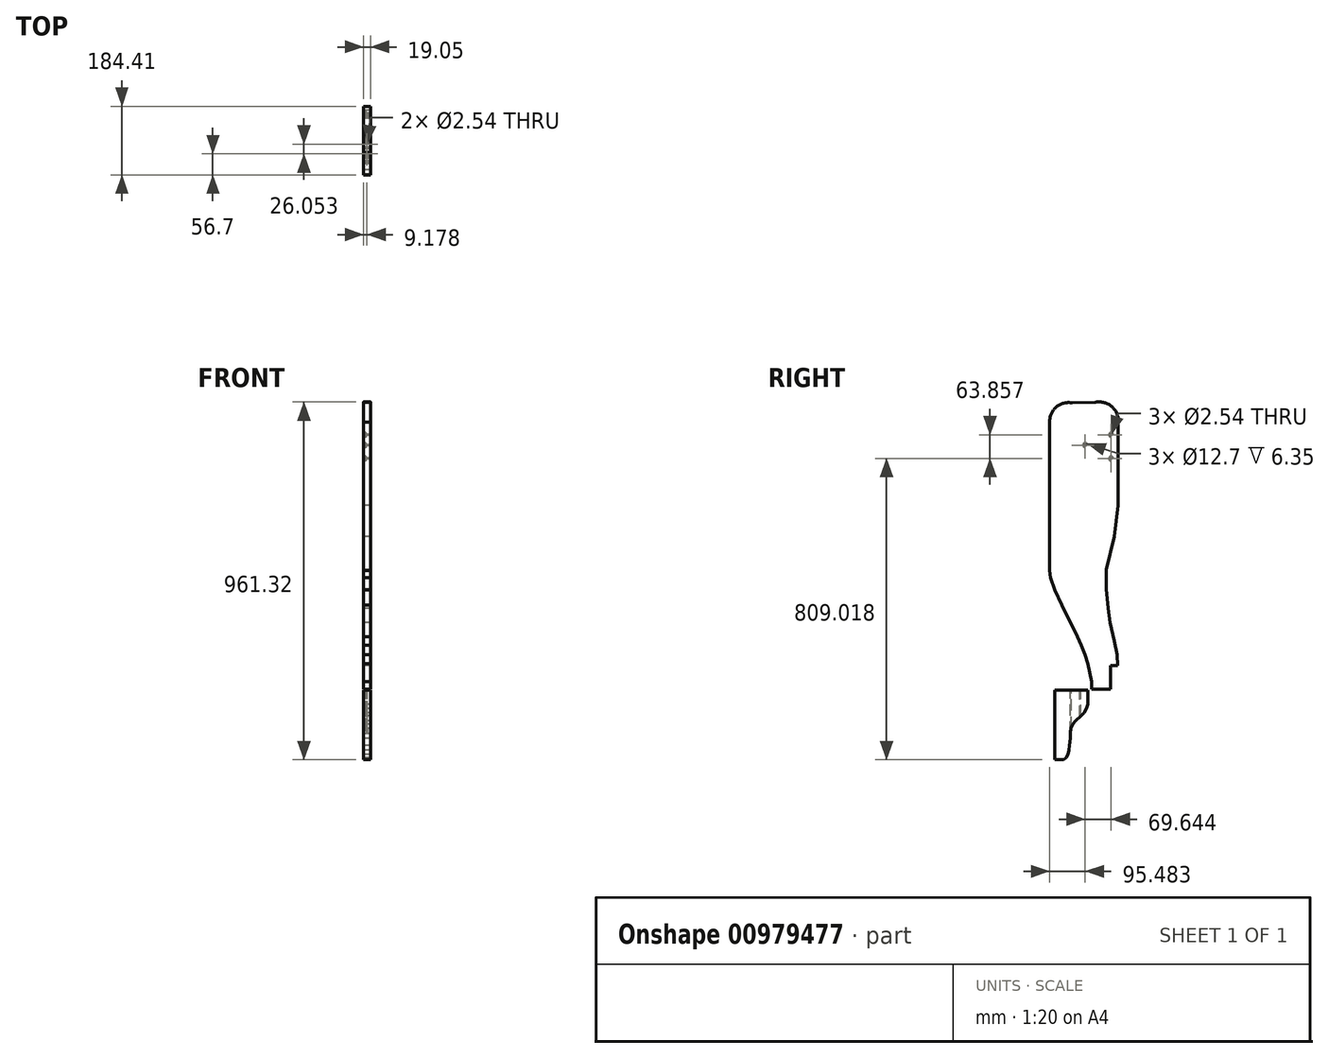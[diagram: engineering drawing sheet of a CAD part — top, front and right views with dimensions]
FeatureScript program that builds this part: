
annotation { "Feature Type Name" : "Feature", "Feature Type Description" : "" }
export const myFeature = defineFeature(function(context is Context, id is Id, definition is map)
    precondition{}
    {
        {
            var Q0;
            Q0=qCreatedBy(makeId("Right.planeOp"),FACE);
            var sketch = newSketch(context, id + "F0", { "sketchPlane" : qUnion([Q0])});
            skArc(sketch, "E0", {"start": v(-9.46, 75.88) * mm, "mid": v(-26, 118.46) * mm, "end": v(-70.06, 130.54) * mm});
            skArc(sketch, "E1", {"start": v(-132.5, 128.84) * mm, "mid": v(-175.59, 117.94) * mm, "end": v(-193.61, 77.32) * mm});
            skLineSegment(sketch, "E2", {"start": v(-70.06, 130.54) * mm, "end": v(-132.5, 128.84) * mm});
            skLineSegment(sketch, "E3", {"start": v(-9.46, -145.88) * mm, "end": v(-9.46, 75.88) * mm});
            skLineSegment(sketch, "E4", {"start": v(-193.61, 77.32) * mm, "end": v(-193.61, -321.25) * mm});
            skLineSegment(sketch, "E5", {"start": v(-10.8, -577.01) * mm, "end": v(-29.84, -577.01) * mm});
            skLineSegment(sketch, "E6", {"start": v(-9.46, -145.88) * mm, "end": v(-19.66, -230.65) * mm});
            skLineSegment(sketch, "E7", {"start": v(-19.66, -230.65) * mm, "end": v(-41.21, -318.93) * mm});
            skLineSegment(sketch, "E8", {"start": v(-41.21, -318.93) * mm, "end": v(-41.21, -370.76) * mm});
            skLineSegment(sketch, "E9", {"start": v(-41.21, -370.76) * mm, "end": v(-36.8, -423.85) * mm});
            skLineSegment(sketch, "E10", {"start": v(-36.8, -423.85) * mm, "end": v(-30.98, -461.78) * mm});
            skLineSegment(sketch, "E11", {"start": v(-30.98, -461.78) * mm, "end": v(-20.05, -510.64) * mm});
            skLineSegment(sketch, "E12", {"start": v(-20.05, -510.64) * mm, "end": v(-12.2, -547.2) * mm});
            skLineSegment(sketch, "E13", {"start": v(-12.2, -547.2) * mm, "end": v(-10.8, -577.01) * mm});
            skLineSegment(sketch, "E14", {"start": v(-29.84, -640.51) * mm, "end": v(-29.84, -577.01) * mm});
            skLineSegment(sketch, "E15", {"start": v(-87.3, -588.8) * mm, "end": v(-91.04, -571.55) * mm});
            skLineSegment(sketch, "E16", {"start": v(-91.04, -571.55) * mm, "end": v(-98.51, -548.28) * mm});
            skLineSegment(sketch, "E17", {"start": v(-98.51, -548.28) * mm, "end": v(-108.2, -522.94) * mm});
            skLineSegment(sketch, "E18", {"start": v(-108.2, -522.94) * mm, "end": v(-119.14, -499.02) * mm});
            skLineSegment(sketch, "E19", {"start": v(-119.14, -499.02) * mm, "end": v(-161.16, -414.63) * mm});
            skLineSegment(sketch, "E20", {"start": v(-161.16, -414.63) * mm, "end": v(-179.94, -373.8) * mm});
            skLineSegment(sketch, "E21", {"start": v(-179.94, -373.8) * mm, "end": v(-190.87, -340.66) * mm});
            skLineSegment(sketch, "E22", {"start": v(-190.87, -340.66) * mm, "end": v(-193.61, -321.25) * mm});
            skLineSegment(sketch, "E23", {"start": v(-101.28, 129.69) * mm, "end": v(-98.16, 15.43) * mm, "construction": true});
            skLineSegment(sketch, "E24", {"start": v(-98.16, 15.43) * mm, "end": v(-9.46, 17.85) * mm, "construction": true});
            skLineSegment(sketch, "E25", {"start": v(-9.46, 43.1) * mm, "end": v(-28.51, 43.1) * mm, "construction": true});
            skPoint(sketch, "E26", {"position": v(-28.34, 17.34) * mm});
            skPoint(sketch, "E27", {"position": v(-53.8, 16.64) * mm});
            skPoint(sketch, "E28", {"position": v(-88.41, 15.7) * mm});
            skPoint(sketch, "E29", {"position": v(-28.51, -20.76) * mm});
            skLineSegment(sketch, "E30", {"start": v(-98.16, 15.43) * mm, "end": v(-193.61, 12.83) * mm, "construction": true});
            skLineSegment(sketch, "E31", {"start": v(-193.61, 12.83) * mm, "end": v(-142.83, 14.21) * mm});
            skPoint(sketch, "E32", {"position": v(-142.83, 14.21) * mm});
            skLineSegment(sketch, "E33", {"start": v(-87.3, -588.8) * mm, "end": v(-80.64, -619.55) * mm});
            skLineSegment(sketch, "E34", {"start": v(-80.64, -619.55) * mm, "end": v(-80.64, -619.82) * mm});
            skLineSegment(sketch, "E35", {"start": v(-80.64, -619.82) * mm, "end": v(-80.64, -629.6) * mm});
            skLineSegment(sketch, "E36", {"start": v(-80.64, -629.6) * mm, "end": v(-80.64, -640.44) * mm});
            skLineSegment(sketch, "E37", {"start": v(-80.64, -640.44) * mm, "end": v(-29.84, -640.51) * mm});
            skSolve(sketch);
        }
        {
            var Q0;
            Q0=qSketchRegion(id+"F0",true);
            extrude(context, id + "F1", {"entities" : qUnion([Q0]), "depth" : 19.05 * mm});
        }
        {
            var Q0;
            Q0=qCreatedBy(makeId("Right.planeOp"),FACE);
            var sketch = newSketch(context, id + "F2", { "sketchPlane" : qUnion([Q0])});
            skLineSegment(sketch, "E38", {"start": v(-91.54, -643.6) * mm, "end": v(-180.44, -643.6) * mm});
            skLineSegment(sketch, "E39", {"start": v(-180.44, -643.6) * mm, "end": v(-180.44, -829.78) * mm});
            skLineSegment(sketch, "E40", {"start": v(-180.44, -829.78) * mm, "end": v(-163.7, -829.78) * mm});
            skLineSegment(sketch, "E41", {"start": v(-91.54, -643.6) * mm, "end": v(-91.54, -681.07) * mm});
            skLineSegment(sketch, "E42", {"start": v(-91.54, -681.07) * mm, "end": v(-94.58, -691.9) * mm});
            skLineSegment(sketch, "E43", {"start": v(-94.58, -691.9) * mm, "end": v(-101.21, -703.64) * mm});
            skLineSegment(sketch, "E44", {"start": v(-101.21, -703.64) * mm, "end": v(-108.9, -711.93) * mm});
            skLineSegment(sketch, "E45", {"start": v(-108.9, -711.93) * mm, "end": v(-123.5, -725.03) * mm});
            skLineSegment(sketch, "E46", {"start": v(-123.5, -725.03) * mm, "end": v(-131.33, -734.22) * mm});
            skLineSegment(sketch, "E47", {"start": v(-131.33, -734.22) * mm, "end": v(-136.6, -745.78) * mm});
            skLineSegment(sketch, "E48", {"start": v(-136.6, -745.78) * mm, "end": v(-138.5, -759.4) * mm});
            skLineSegment(sketch, "E49", {"start": v(-138.5, -759.4) * mm, "end": v(-138.5, -773.04) * mm});
            skLineSegment(sketch, "E50", {"start": v(-138.5, -773.04) * mm, "end": v(-140.18, -791.2) * mm});
            skLineSegment(sketch, "E51", {"start": v(-140.18, -791.2) * mm, "end": v(-142.1, -803.88) * mm});
            skLineSegment(sketch, "E52", {"start": v(-142.1, -803.88) * mm, "end": v(-144.72, -815.35) * mm});
            skLineSegment(sketch, "E53", {"start": v(-144.72, -815.35) * mm, "end": v(-149.5, -824.2) * mm});
            skLineSegment(sketch, "E54", {"start": v(-149.5, -824.2) * mm, "end": v(-155.48, -829.46) * mm});
            skLineSegment(sketch, "E55", {"start": v(-155.48, -829.46) * mm, "end": v(-163.7, -829.78) * mm});
            skSolve(sketch);
        }
        {
            var Q0;
            Q0=qSketchRegion(id+"F2",true);
            extrude(context, id + "F3", {"entities" : qUnion([Q0]), "depth" : 19.05 * mm});
        }
        {
            var Q0;
            Q0=makeQuery(id+"F3.opExtrude","SWEPT_FACE",FACE,{"disambiguationData":[OSD([sQuery(id+"F2.wireOp",EDGE,"E38")])]});
            var sketch = newSketch(context, id + "F4", { "sketchPlane" : qUnion([Q0])});
            skPoint(sketch, "E56", {"position": v(9.18, -110.89) * mm});
            skPoint(sketch, "E57", {"position": v(9.18, -136.94) * mm});
            skLineSegment(sketch, "E58", {"start": v(9.53, -180.44) * mm, "end": v(9.18, -91.54) * mm, "construction": true});
            skSolve(sketch);
        }
        {
            var Q0;
            Q0=sQuery(id+"F4.wireOp",VERTEX,"E57");
            var Q1;
            Q1=sQuery(id+"F4.wireOp",VERTEX,"E56");
            var Q2;
            Q2=makeQuery(id+"F3.opExtrude","SWEPT_BODY",BODY,{"disambiguationData":[OSD([sQuery(id+"F2.wireOp",EDGE,"E38"),sQuery(id+"F2.wireOp",EDGE,"E39"),sQuery(id+"F2.wireOp",EDGE,"E40"),sQuery(id+"F2.wireOp",EDGE,"E41"),sQuery(id+"F2.wireOp",EDGE,"E42"),sQuery(id+"F2.wireOp",EDGE,"E43"),sQuery(id+"F2.wireOp",EDGE,"E44"),sQuery(id+"F2.wireOp",EDGE,"E45"),sQuery(id+"F2.wireOp",EDGE,"E46"),sQuery(id+"F2.wireOp",EDGE,"E47"),sQuery(id+"F2.wireOp",EDGE,"E48"),sQuery(id+"F2.wireOp",EDGE,"E49"),sQuery(id+"F2.wireOp",EDGE,"E50"),sQuery(id+"F2.wireOp",EDGE,"E51"),sQuery(id+"F2.wireOp",EDGE,"E52"),sQuery(id+"F2.wireOp",EDGE,"E53"),sQuery(id+"F2.wireOp",EDGE,"E54"),sQuery(id+"F2.wireOp",EDGE,"E55")])]});
            hole(context, id + "F5", {"style" : HoleStyle.SIMPLE, "endStyle" : HoleEndStyle.THROUGH, "holeDiameter" : 2.54 * mm, "locations" : qUnion([Q0, Q1]), "scope" : qUnion([Q2]), "isTappedThrough" : true});
        }
        {
            var Q0;
            Q0=sQuery(id+"F0.wireOp",VERTEX,"E29");
            var Q1;
            Q1=sQuery(id+"F0.wireOp",VERTEX,"E25.end");
            var Q2;
            Q2=sQuery(id+"F0.wireOp",VERTEX,"E23.end");
            var Q3;
            Q3=makeQuery(id+"F1.opExtrude","SWEPT_BODY",BODY,{"disambiguationData":[OSD([sQuery(id+"F0.wireOp",EDGE,"E0"),sQuery(id+"F0.wireOp",EDGE,"E1"),sQuery(id+"F0.wireOp",EDGE,"E2"),sQuery(id+"F0.wireOp",EDGE,"E3"),sQuery(id+"F0.wireOp",EDGE,"E4"),sQuery(id+"F0.wireOp",EDGE,"E5"),sQuery(id+"F0.wireOp",EDGE,"oIR5Aljz-vCWG-jUG9-CAz4-xxcIfngGmacA"),sQuery(id+"F0.wireOp",EDGE,"2AJYBhot-aTbF-qlyU-3KPI-1kneUEEkDNKH"),sQuery(id+"F0.wireOp",EDGE,"E6"),sQuery(id+"F0.wireOp",EDGE,"E7"),sQuery(id+"F0.wireOp",EDGE,"E8"),sQuery(id+"F0.wireOp",EDGE,"E9"),sQuery(id+"F0.wireOp",EDGE,"E10"),sQuery(id+"F0.wireOp",EDGE,"E11"),sQuery(id+"F0.wireOp",EDGE,"E12"),sQuery(id+"F0.wireOp",EDGE,"E13"),sQuery(id+"F0.wireOp",EDGE,"E14"),sQuery(id+"F0.wireOp",EDGE,"ePQwNw62-HjoT-TKd1-s3V2-jpgCmGEpgwtA"),sQuery(id+"F0.wireOp",EDGE,"E15"),sQuery(id+"F0.wireOp",EDGE,"E16"),sQuery(id+"F0.wireOp",EDGE,"E17"),sQuery(id+"F0.wireOp",EDGE,"E18"),sQuery(id+"F0.wireOp",EDGE,"E19"),sQuery(id+"F0.wireOp",EDGE,"E20"),sQuery(id+"F0.wireOp",EDGE,"E21"),sQuery(id+"F0.wireOp",EDGE,"E22")])]});
            hole(context, id + "F6", {"style" : HoleStyle.C_BORE, "endStyle" : HoleEndStyle.THROUGH, "oppositeDirection" : true, "holeDiameter" : 2.54 * mm, "cBoreDiameter" : 12.7 * mm, "cBoreDepth" : 6.35 * mm, "locations" : qUnion([Q0, Q1, Q2]), "scope" : qUnion([Q3]), "isTappedThrough" : true});
        }
    });
